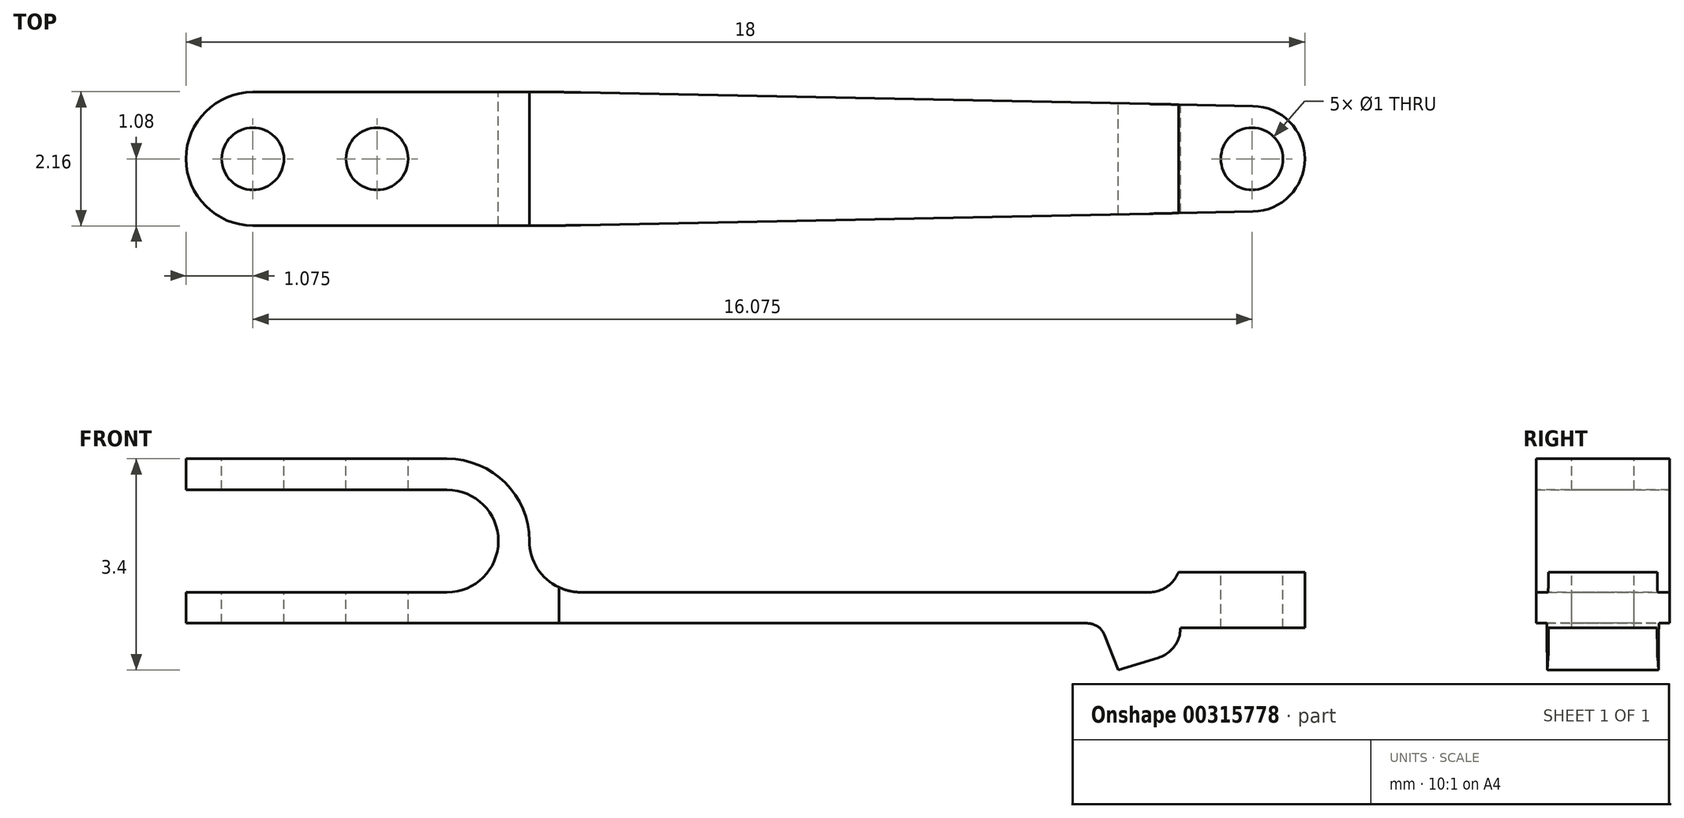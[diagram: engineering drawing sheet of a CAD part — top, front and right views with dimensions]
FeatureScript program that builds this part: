
annotation { "Feature Type Name" : "Feature", "Feature Type Description" : "" }
export const myFeature = defineFeature(function(context is Context, id is Id, definition is map)
    precondition{}
    {
        {
            var Q0;
            Q0=qCreatedBy(makeId("Front.planeOp"),FACE);
            var sketch = newSketch(context, id + "F0", { "sketchPlane" : qUnion([Q0])});
            skLineSegment(sketch, "E0", {"start": v(0, 0) * mm, "end": v(14.5, 0) * mm});
            skLineSegment(sketch, "E1.0", {"start": v(0, 0.5) * mm, "end": v(4.2, 0.5) * mm});
            skLineSegment(sketch, "E2.0", {"start": v(0, 2.15) * mm, "end": v(5.24, 2.15) * mm});
            skLineSegment(sketch, "E3.0", {"start": v(0, 2.65) * mm, "end": v(4.2, 2.65) * mm});
            skArc(sketch, "E4", {"start": v(4.2, 0.5) * mm, "mid": v(5.03, 1.32) * mm, "end": v(4.2, 2.15) * mm});
            skLineSegment(sketch, "E5", {"start": v(5.53, 1.32) * mm, "end": v(5.53, 1.32) * mm});
            skArc(sketch, "E6.trimOffspring", {"start": v(5.53, 1.32) * mm, "mid": v(5.14, 2.26) * mm, "end": v(4.2, 2.65) * mm});
            skLineSegment(sketch, "E7.trimOffspring", {"start": v(6.35, 0.5) * mm, "end": v(15.5, 0.5) * mm});
            skArc(sketch, "E8.filletArc", {"start": v(5.53, 1.32) * mm, "mid": v(5.77, 0.74) * mm, "end": v(6.35, 0.5) * mm});
            skLineSegment(sketch, "E9", {"start": v(0, 2.65) * mm, "end": v(0, 2.15) * mm});
            skLineSegment(sketch, "E10", {"start": v(0, 0.5) * mm, "end": v(0, 0) * mm});
            skPoint(sketch, "E11.orphan", {"position": v(4.2, 3.28) * mm});
            skLineSegment(sketch, "E12", {"start": v(18, 0.83) * mm, "end": v(18, -0.07) * mm});
            skLineSegment(sketch, "E13", {"start": v(18, 0.83) * mm, "end": v(15.97, 0.83) * mm});
            skLineSegment(sketch, "E14.0", {"start": v(18, -0.07) * mm, "end": v(16, -0.07) * mm});
            skLineSegment(sketch, "E15", {"start": v(16, -0.07) * mm, "end": v(16, -0.08) * mm});
            skLineSegment(sketch, "E16", {"start": v(15, -0.75) * mm, "end": v(14.78, -0.19) * mm});
            skPoint(sketch, "E17.visualSharp", {"position": v(16, 0.5) * mm});
            skArc(sketch, "E17.filletArc", {"start": v(15.5, 0.5) * mm, "mid": v(15.79, 0.59) * mm, "end": v(15.97, 0.83) * mm});
            skPoint(sketch, "E18.newPointA", {"position": v(14.86, 0) * mm});
            skArc(sketch, "E18.filletArc", {"start": v(14.78, -0.19) * mm, "mid": v(14.67, -0.05) * mm, "end": v(14.5, 0) * mm});
            skLineSegment(sketch, "E19", {"start": v(16, -0.07) * mm, "end": v(16, -0.07) * mm});
            skLineSegment(sketch, "E20", {"start": v(15, -0.75) * mm, "end": v(15.65, -0.55) * mm});
            skArc(sketch, "E21.filletArc", {"start": v(15.65, -0.55) * mm, "mid": v(15.9, -0.37) * mm, "end": v(16, -0.07) * mm});
            skSolve(sketch);
        }
        {
            var Q0;
            Q0 = qSketchRegion(id + "F0", true);
            extrude(context, id + "F1", {"entities" : qUnion([Q0]), "endBound" : BoundingType.SYMMETRIC, "depth" : 2.15 * mm});
        }
        {
            var Q0;
            Q0=qCreatedBy(makeId("Top.planeOp"),FACE);
            var sketch = newSketch(context, id + "F2", { "sketchPlane" : qUnion([Q0])});
            skLineSegment(sketch, "E22", {"start": v(18, 0) * mm, "end": v(18, 0) * mm});
            skLineSegment(sketch, "E23", {"start": v(17.17, 0.85) * mm, "end": v(6, 1.08) * mm});
            skLineSegment(sketch, "E24", {"start": v(6, 1.08) * mm, "end": v(1.08, 1.08) * mm});
            skLineSegment(sketch, "E25", {"start": v(0, 0) * mm, "end": v(0, 0) * mm});
            skPoint(sketch, "E26.visualSharp", {"position": v(0, 1.08) * mm});
            skArc(sketch, "E26.filletArc", {"start": v(1.08, 1.08) * mm, "mid": v(0.31, 0.76) * mm, "end": v(0, 0) * mm});
            skPoint(sketch, "E27.visualSharp", {"position": v(18, 0.83) * mm});
            skArc(sketch, "E27.filletArc", {"start": v(18, 0) * mm, "mid": v(17.76, 0.6) * mm, "end": v(17.17, 0.85) * mm});
            skCircle(sketch, "E28", {"center": v(1.08, 0) * mm, "radius": 0.5 * mm});
            skCircle(sketch, "E29", {"center": v(3.08, 0) * mm, "radius": 0.5 * mm});
            skCircle(sketch, "E30", {"center": v(17.15, 0) * mm, "radius": 0.5 * mm});
            skLineSegment(sketch, "E31.MirrorCS", {"start": v(6, -1.08) * mm, "end": v(1.08, -1.08) * mm});
            skLineSegment(sketch, "E32.MirrorCS", {"start": v(17.17, -0.85) * mm, "end": v(6, -1.08) * mm});
            skArc(sketch, "E33.MirrorCS", {"start": v(1.08, -1.08) * mm, "mid": v(0.31, -0.76) * mm, "end": v(0, 0) * mm});
            skArc(sketch, "E34.MirrorCS", {"start": v(18, 0) * mm, "mid": v(17.76, -0.6) * mm, "end": v(17.17, -0.85) * mm});
            skLineSegment(sketch, "E35.bottom", {"start": v(-1.97, -2.96) * mm, "end": v(18.95, -2.96) * mm});
            skLineSegment(sketch, "E35.top", {"start": v(-1.97, 2.85) * mm, "end": v(18.95, 2.85) * mm});
            skLineSegment(sketch, "E35.left", {"start": v(-1.97, -2.96) * mm, "end": v(-1.97, 2.85) * mm});
            skLineSegment(sketch, "E35.right", {"start": v(18.95, -2.96) * mm, "end": v(18.95, 2.85) * mm});
            skSolve(sketch);
        }
        {
            var Q0;
            Q0=makeQuery(id+"F2.imprint","IMPRINT",FACE,{"disambiguationData":[TD([[makeQuery(id+"F2.imprint","IMPRINT",EDGE,{"derivedFrom":sQuery(id+"F2.wireOp",EDGE,"E23")}),-1.0]])]});
            var Q1;
            Q1=makeQuery(id+"F2.imprint","IMPRINT",FACE,{"disambiguationData":[TD([[makeQuery(id+"F2.imprint","IMPRINT",EDGE,{"derivedFrom":sQuery(id+"F2.wireOp",EDGE,"E28")}),1.0]])]});
            var Q2;
            Q2=makeQuery(id+"F2.imprint","IMPRINT",FACE,{"disambiguationData":[TD([[makeQuery(id+"F2.imprint","IMPRINT",EDGE,{"derivedFrom":sQuery(id+"F2.wireOp",EDGE,"E29")}),1.0]])]});
            extrude(context, id + "F3", {"entities" : qUnion([Q0, Q1, Q2]), "operationType" : NewBodyOperationType.REMOVE, "endBound" : BoundingType.SYMMETRIC, "oppositeDirection" : true, "depth" : 25 * mm});
        }
        {
            var Q0;
            Q0=qCreatedBy(makeId("Top.planeOp"),FACE);
            var sketch = newSketch(context, id + "F4", { "sketchPlane" : qUnion([Q0])});
            skCircle(sketch, "E36", {"center": v(17.15, 0) * mm, "radius": 0.5 * mm});
            skSolve(sketch);
        }
        {
            var Q0;
            Q0 = qSketchRegion(id + "F4", true);
            extrude(context, id + "F5", {"entities" : qUnion([Q0]), "operationType" : NewBodyOperationType.REMOVE, "endBound" : BoundingType.SYMMETRIC, "oppositeDirection" : true, "depth" : 25 * mm});
        }
    });
